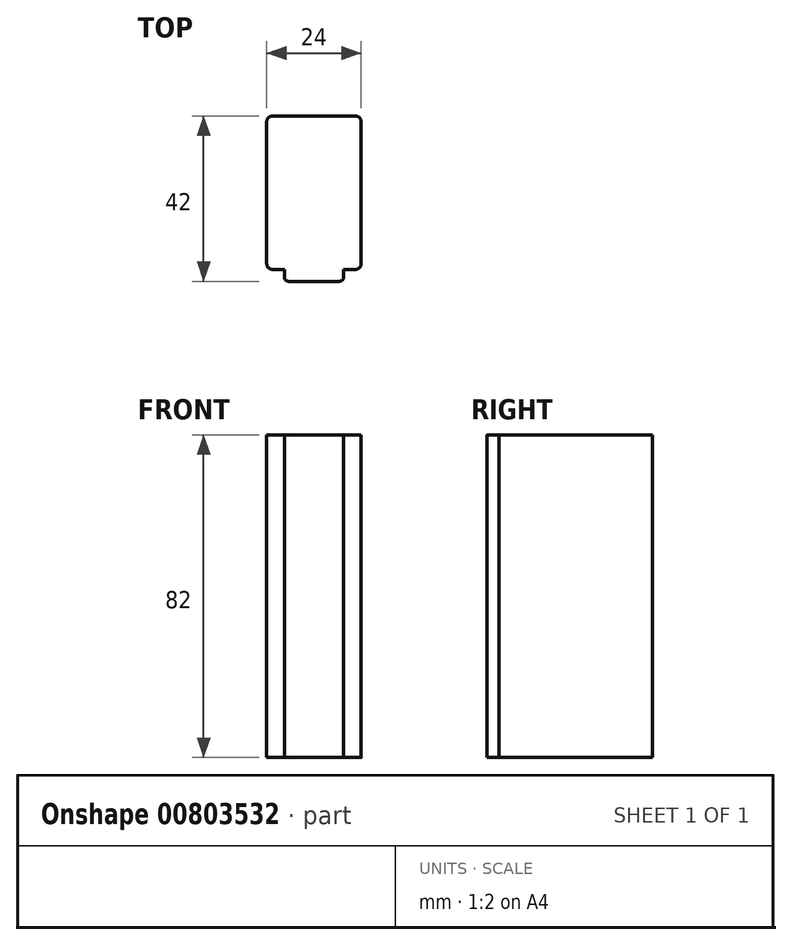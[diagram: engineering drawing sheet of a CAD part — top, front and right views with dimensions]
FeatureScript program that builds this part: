
annotation { "Feature Type Name" : "Feature", "Feature Type Description" : "" }
export const myFeature = defineFeature(function(context is Context, id is Id, definition is map)
    precondition{}
    {
        {
            var Q0;
            Q0=qCreatedBy(makeId("Top.planeOp"),FACE);
            var sketch = newSketch(context, id + "F0", { "sketchPlane" : qUnion([Q0])});
            skLineSegment(sketch, "E0.bottom", {"start": v(-10.5, 19.5) * mm, "end": v(10.5, 19.5) * mm});
            skLineSegment(sketch, "E0.top", {"start": v(-10.5, -19.5) * mm, "end": v(-7.5, -19.5) * mm});
            skLineSegment(sketch, "E0.left", {"start": v(-12, 18) * mm, "end": v(-12, -18) * mm});
            skLineSegment(sketch, "E0.right", {"start": v(12, 18) * mm, "end": v(12, -18) * mm});
            skPoint(sketch, "E0.middle", {"position": v(0, 0) * mm});
            skLineSegment(sketch, "E1.bottom", {"start": v(6.5, -22.5) * mm, "end": v(-6.5, -22.5) * mm});
            skLineSegment(sketch, "E1.left", {"start": v(7.5, -21.5) * mm, "end": v(7.5, -19.5) * mm});
            skLineSegment(sketch, "E1.right", {"start": v(-7.5, -21.5) * mm, "end": v(-7.5, -19.5) * mm});
            skPoint(sketch, "E1.middle", {"position": v(0, -19.5) * mm});
            skPoint(sketch, "E2.orphan", {"position": v(-7.5, -16.5) * mm});
            skPoint(sketch, "E3.orphan", {"position": v(7.5, -16.5) * mm});
            skLineSegment(sketch, "E4.trimOffspring", {"start": v(7.5, -19.5) * mm, "end": v(10.5, -19.5) * mm});
            skPoint(sketch, "E5.visualSharp", {"position": v(-12, 19.5) * mm});
            skArc(sketch, "E5.filletArc", {"start": v(-10.5, 19.5) * mm, "mid": v(-11.56, 19.06) * mm, "end": v(-12, 18) * mm});
            skPoint(sketch, "E6.visualSharp", {"position": v(12, 19.5) * mm});
            skArc(sketch, "E6.filletArc", {"start": v(12, 18) * mm, "mid": v(11.56, 19.06) * mm, "end": v(10.5, 19.5) * mm});
            skPoint(sketch, "E7.visualSharp", {"position": v(-12, -19.5) * mm});
            skArc(sketch, "E7.filletArc", {"start": v(-12, -18) * mm, "mid": v(-11.56, -19.06) * mm, "end": v(-10.5, -19.5) * mm});
            skPoint(sketch, "E8.visualSharp", {"position": v(12, -19.5) * mm});
            skArc(sketch, "E8.filletArc", {"start": v(10.5, -19.5) * mm, "mid": v(11.56, -19.06) * mm, "end": v(12, -18) * mm});
            skPoint(sketch, "E9.visualSharp", {"position": v(-7.5, -22.5) * mm});
            skArc(sketch, "E9.filletArc", {"start": v(-7.5, -21.5) * mm, "mid": v(-7.2, -22.2) * mm, "end": v(-6.5, -22.5) * mm});
            skPoint(sketch, "E10.visualSharp", {"position": v(7.5, -22.5) * mm});
            skArc(sketch, "E10.filletArc", {"start": v(6.5, -22.5) * mm, "mid": v(7.2, -22.2) * mm, "end": v(7.5, -21.5) * mm});
            skSolve(sketch);
        }
        {
            var Q0;
            Q0 = qSketchRegion(id + "F0", true);
            extrude(context, id + "F1", {"entities" : qUnion([Q0]), "depth" : 82 * mm, "offsetDistance" : 25 * mm});
        }
    });
